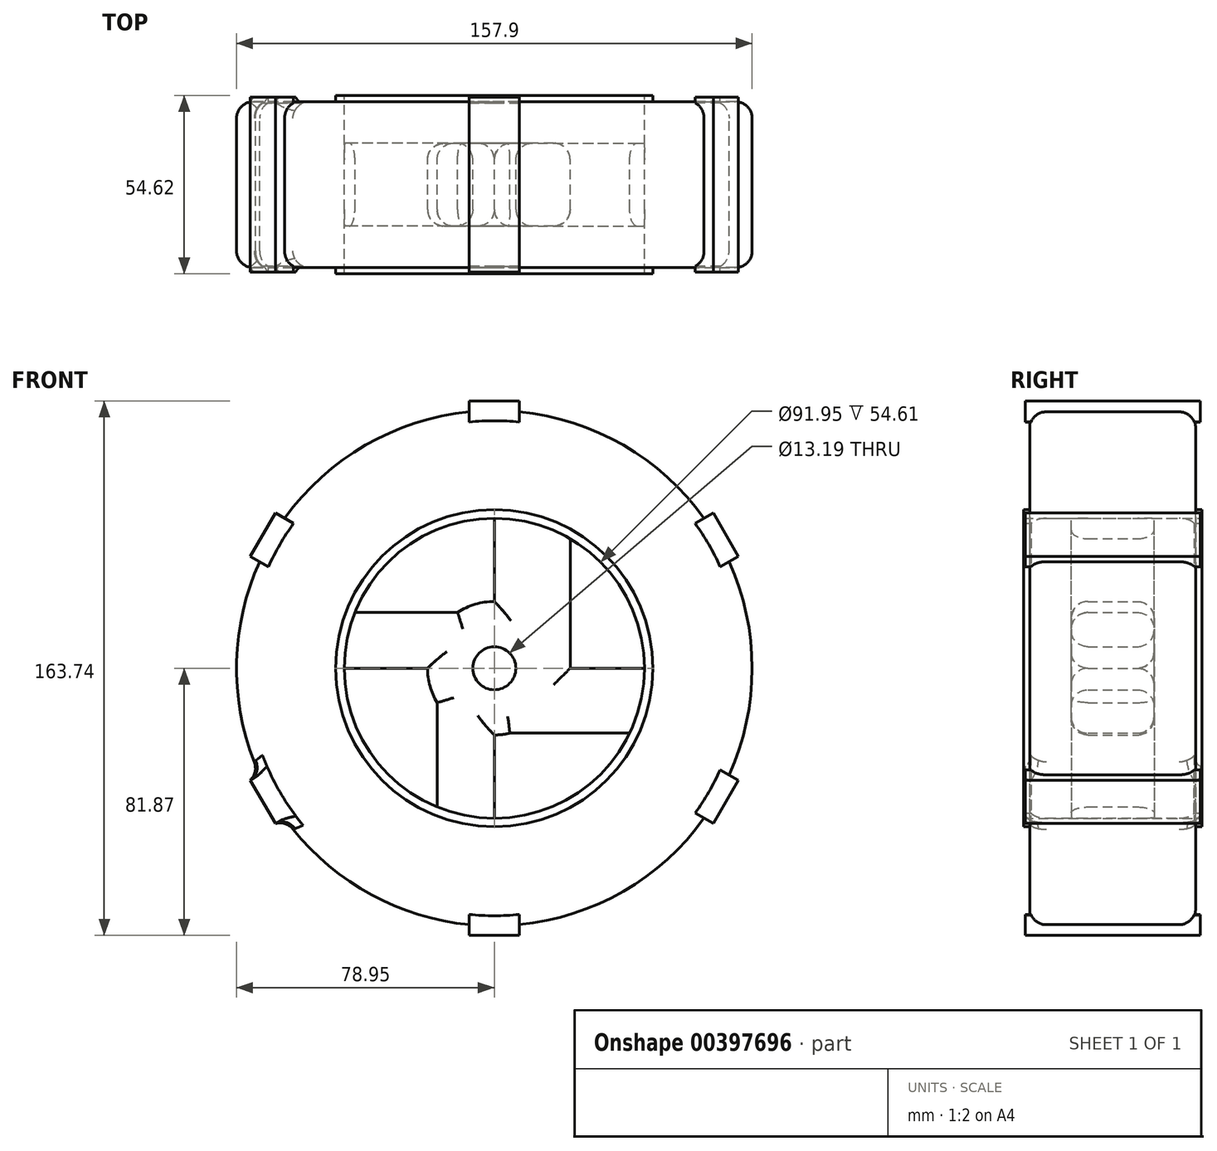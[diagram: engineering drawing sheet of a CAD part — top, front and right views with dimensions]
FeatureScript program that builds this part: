
annotation { "Feature Type Name" : "Feature", "Feature Type Description" : "" }
export const myFeature = defineFeature(function(context is Context, id is Id, definition is map)
    precondition{}
    {
        {
            var Q0;
            Q0=qCreatedBy(makeId("Front.planeOp"),FACE);
            var sketch = newSketch(context, id + "F0", { "sketchPlane" : qUnion([Q0])});
            skCircle(sketch, "E0", {"center": v(0, 0) * mm, "radius": 46.7 * mm});
            skCircle(sketch, "E1", {"center": v(0, 0) * mm, "radius": 78.95 * mm});
            skSolve(sketch);
        }
        {
            var Q0;
            Q0=makeQuery(id+"F0.imprint","IMPRINT",FACE,{"disambiguationData":[TD([[makeQuery(id+"F0.imprint","IMPRINT",EDGE,{"derivedFrom":sQuery(id+"F0.wireOp",EDGE,"E0")}),-1.0]])]});
            extrude(context, id + "F1", {"entities" : qUnion([Q0]), "endBound" : BoundingType.SYMMETRIC, "depth" : 50.8 * mm, "offsetDistance" : 25.4 * mm});
        }
        {
            var Q0;
            Q0=makeQuery(id+"F1.opExtrude","CAP_EDGE",EDGE,{"disambiguationData":[OSD([sQuery(id+"F0.wireOp",EDGE,"E1")])],"isStart":false});
            var Q1;
            Q1=makeQuery(id+"F1.opExtrude","SWEPT_FACE",FACE,{"disambiguationData":[OSD([sQuery(id+"F0.wireOp",EDGE,"E1")])]});
            fillet(context, id + "F2", {"entities" : qUnion([Q0, Q1]), "radius" : 5.08 * mm, "tangentPropagation" : true, "allowEdgeOverflow" : false});
        }
        {
            var Q0;
            Q0=qCreatedBy(makeId("Front.planeOp"),FACE);
            var sketch = newSketch(context, id + "F3", { "sketchPlane" : qUnion([Q0])});
            skCircle(sketch, "E2", {"center": v(0, 0) * mm, "radius": 48.57 * mm});
            skCircle(sketch, "E3", {"center": v(0, 0) * mm, "radius": 45.98 * mm});
            skSolve(sketch);
        }
        {
            var Q0;
            Q0 = qSketchRegion(id + "F3", true);
            extrude(context, id + "F4", {"entities" : qUnion([Q0]), "operationType" : NewBodyOperationType.ADD, "endBound" : BoundingType.SYMMETRIC, "depth" : 54.6 * mm, "offsetDistance" : 25.4 * mm});
        }
        {
            var Q0;
            Q0=qCreatedBy(makeId("Front.planeOp"),FACE);
            var sketch = newSketch(context, id + "F5", { "sketchPlane" : qUnion([Q0])});
            skCircle(sketch, "E4", {"center": v(0, 0) * mm, "radius": 20.45 * mm});
            skCircle(sketch, "E5", {"center": v(0, 0) * mm, "radius": 6.6 * mm});
            skLineSegment(sketch, "E6.bottom", {"start": v(0, 0) * mm, "end": v(53.17, 0) * mm});
            skLineSegment(sketch, "E6.top", {"start": v(0, -19.9) * mm, "end": v(53.17, -19.9) * mm});
            skLineSegment(sketch, "E6.left", {"start": v(0, 0) * mm, "end": v(0, -19.9) * mm});
            skLineSegment(sketch, "E6.right", {"start": v(53.17, 0) * mm, "end": v(53.17, -19.9) * mm});
            skLineSegment(sketch, "E7.bottom", {"start": v(0, 0) * mm, "end": v(-49.35, 0) * mm});
            skLineSegment(sketch, "E7.top", {"start": v(0, 17.09) * mm, "end": v(-49.35, 17.09) * mm});
            skLineSegment(sketch, "E7.left", {"start": v(0, 0) * mm, "end": v(0, 17.09) * mm});
            skLineSegment(sketch, "E7.right", {"start": v(-49.35, 0) * mm, "end": v(-49.35, 17.09) * mm});
            skLineSegment(sketch, "E8.bottom", {"start": v(0, 0) * mm, "end": v(-17.53, 0) * mm});
            skLineSegment(sketch, "E8.top", {"start": v(0, -48.72) * mm, "end": v(-17.53, -48.72) * mm});
            skLineSegment(sketch, "E8.left", {"start": v(0, 0) * mm, "end": v(0, -48.72) * mm});
            skLineSegment(sketch, "E8.right", {"start": v(-17.53, 0) * mm, "end": v(-17.53, -48.72) * mm});
            skLineSegment(sketch, "E9.bottom", {"start": v(0, 0) * mm, "end": v(23.22, 0) * mm});
            skLineSegment(sketch, "E9.top", {"start": v(0, 56.09) * mm, "end": v(23.22, 56.09) * mm});
            skLineSegment(sketch, "E9.left", {"start": v(0, 0) * mm, "end": v(0, 56.09) * mm});
            skLineSegment(sketch, "E9.right", {"start": v(23.22, 0) * mm, "end": v(23.22, 56.09) * mm});
            skSolve(sketch);
        }
        {
            var Q0;
            Q0 = qSketchRegion(id + "F5", true);
            extrude(context, id + "F6", {"entities" : qUnion([Q0]), "operationType" : NewBodyOperationType.ADD, "endBound" : BoundingType.SYMMETRIC, "depth" : 25.4 * mm, "offsetDistance" : 25.4 * mm});
        }
        {
            var Q0;
            Q0=makeQuery(id+"F6.opExtrude","CAP_EDGE",EDGE,{"disambiguationData":[OSD([sQuery(id+"F5.wireOp",EDGE,"E7.top")])],"isStart":false});
            var Q1;
            {var subQ0=sQuery(id+"F5.wireOp",EDGE,"E4");Q1=makeQuery(id+"F6.opExtrude","CAP_EDGE",EDGE,{"disambiguationData":[OSD([subQ0]),TDD([makeQuery(id+"F5.imprint","IMPRINT",EDGE,{"disambiguationData":[TD([[makeQuery(id+"F5.imprint","INTERSECT",VERTEX,{"derivedFrom":[subQ0,sQuery(id+"F5.wireOp",EDGE,"E9.left")]}),-1.0]])],"derivedFrom":subQ0})])],"isStart":false});}
            var Q2;
            Q2=makeQuery(id+"F6.opExtrude","CAP_EDGE",EDGE,{"disambiguationData":[OSD([sQuery(id+"F5.wireOp",EDGE,"E9.left")])],"isStart":false});
            var Q3;
            Q3=makeQuery(id+"F6.opExtrude","CAP_EDGE",EDGE,{"disambiguationData":[OSD([sQuery(id+"F5.wireOp",EDGE,"E9.right")])],"isStart":false});
            var Q4;
            Q4=makeQuery(id+"F6.opExtrude","CAP_EDGE",EDGE,{"disambiguationData":[OSD([sQuery(id+"F5.wireOp",EDGE,"E6.bottom")])],"isStart":false});
            var Q5;
            Q5=makeQuery(id+"F6.opExtrude","CAP_EDGE",EDGE,{"disambiguationData":[OSD([sQuery(id+"F5.wireOp",EDGE,"E6.top")])],"isStart":false});
            var Q6;
            Q6=makeQuery(id+"F6.opExtrude","CAP_EDGE",EDGE,{"disambiguationData":[OSD([sQuery(id+"F5.wireOp",EDGE,"E8.left")])],"isStart":false});
            var Q7;
            {var subQ0=sQuery(id+"F5.wireOp",EDGE,"E4");Q7=makeQuery(id+"F6.opExtrude","CAP_EDGE",EDGE,{"disambiguationData":[OSD([subQ0]),TDD([makeQuery(id+"F5.imprint","IMPRINT",EDGE,{"disambiguationData":[TD([[makeQuery(id+"F5.imprint","INTERSECT",VERTEX,{"derivedFrom":[subQ0,sQuery(id+"F5.wireOp",EDGE,"E8.left")]}),-1.0]])],"derivedFrom":subQ0})])],"isStart":false});}
            var Q8;
            Q8=makeQuery(id+"F6.opExtrude","CAP_EDGE",EDGE,{"disambiguationData":[OSD([sQuery(id+"F5.wireOp",EDGE,"E8.right")])],"isStart":false});
            var Q9;
            {var subQ0=sQuery(id+"F5.wireOp",EDGE,"E4");Q9=makeQuery(id+"F6.opExtrude","CAP_EDGE",EDGE,{"disambiguationData":[OSD([subQ0]),TDD([makeQuery(id+"F5.imprint","IMPRINT",EDGE,{"disambiguationData":[TD([[makeQuery(id+"F5.imprint","INTERSECT",VERTEX,{"derivedFrom":[subQ0,sQuery(id+"F5.wireOp",EDGE,"E7.bottom")]}),-1.0]])],"derivedFrom":subQ0})])],"isStart":false});}
            var Q10;
            Q10=makeQuery(id+"F6.opExtrude","CAP_EDGE",EDGE,{"disambiguationData":[OSD([sQuery(id+"F5.wireOp",EDGE,"E7.bottom")])],"isStart":false});
            var Q11;
            Q11=makeQuery(id+"F6.opExtrude","CAP_EDGE",EDGE,{"disambiguationData":[OSD([sQuery(id+"F5.wireOp",EDGE,"E9.left")])],"isStart":true});
            var Q12;
            {var subQ0=sQuery(id+"F5.wireOp",EDGE,"E4");Q12=makeQuery(id+"F6.opExtrude","CAP_EDGE",EDGE,{"disambiguationData":[OSD([subQ0]),TDD([makeQuery(id+"F5.imprint","IMPRINT",EDGE,{"disambiguationData":[TD([[makeQuery(id+"F5.imprint","INTERSECT",VERTEX,{"derivedFrom":[subQ0,sQuery(id+"F5.wireOp",EDGE,"E9.left")]}),-1.0]])],"derivedFrom":subQ0})])],"isStart":true});}
            var Q13;
            Q13=makeQuery(id+"F6.opExtrude","CAP_EDGE",EDGE,{"disambiguationData":[OSD([sQuery(id+"F5.wireOp",EDGE,"E7.top")])],"isStart":true});
            var Q14;
            Q14=makeQuery(id+"F6.opExtrude","CAP_EDGE",EDGE,{"disambiguationData":[OSD([sQuery(id+"F5.wireOp",EDGE,"E7.bottom")])],"isStart":true});
            var Q15;
            {var subQ0=sQuery(id+"F5.wireOp",EDGE,"E4");Q15=makeQuery(id+"F6.opExtrude","CAP_EDGE",EDGE,{"disambiguationData":[OSD([subQ0]),TDD([makeQuery(id+"F5.imprint","IMPRINT",EDGE,{"disambiguationData":[TD([[makeQuery(id+"F5.imprint","INTERSECT",VERTEX,{"derivedFrom":[subQ0,sQuery(id+"F5.wireOp",EDGE,"E7.bottom")]}),-1.0]])],"derivedFrom":subQ0})])],"isStart":true});}
            var Q16;
            Q16=makeQuery(id+"F6.opExtrude","CAP_EDGE",EDGE,{"disambiguationData":[OSD([sQuery(id+"F5.wireOp",EDGE,"E8.right")])],"isStart":true});
            var Q17;
            Q17=makeQuery(id+"F6.opExtrude","CAP_EDGE",EDGE,{"disambiguationData":[OSD([sQuery(id+"F5.wireOp",EDGE,"E8.left")])],"isStart":true});
            var Q18;
            {var subQ0=sQuery(id+"F5.wireOp",EDGE,"E4");Q18=makeQuery(id+"F6.opExtrude","CAP_EDGE",EDGE,{"disambiguationData":[OSD([subQ0]),TDD([makeQuery(id+"F5.imprint","IMPRINT",EDGE,{"disambiguationData":[TD([[makeQuery(id+"F5.imprint","INTERSECT",VERTEX,{"derivedFrom":[subQ0,sQuery(id+"F5.wireOp",EDGE,"E8.left")]}),-1.0]])],"derivedFrom":subQ0})])],"isStart":true});}
            var Q19;
            Q19=makeQuery(id+"F6.opExtrude","CAP_EDGE",EDGE,{"disambiguationData":[OSD([sQuery(id+"F5.wireOp",EDGE,"E6.top")])],"isStart":true});
            var Q20;
            Q20=makeQuery(id+"F6.opExtrude","CAP_EDGE",EDGE,{"disambiguationData":[OSD([sQuery(id+"F5.wireOp",EDGE,"E6.bottom")])],"isStart":true});
            var Q21;
            Q21=makeQuery(id+"F6.opExtrude","CAP_EDGE",EDGE,{"disambiguationData":[OSD([sQuery(id+"F5.wireOp",EDGE,"E9.right")])],"isStart":true});
            var Q22;
            Q22=makeQuery(id+"F6.opExtrude","CAP_EDGE",EDGE,{"disambiguationData":[OSD([sQuery(id+"F5.wireOp",EDGE,"E5")])],"isStart":true});
            var Q23;
            Q23=makeQuery(id+"F6.opExtrude","CAP_EDGE",EDGE,{"disambiguationData":[OSD([sQuery(id+"F5.wireOp",EDGE,"E5")])],"isStart":false});
            fillet(context, id + "F7", {"entities" : qUnion([Q0, Q1, Q2, Q3, Q4, Q5, Q6, Q7, Q8, Q9, Q10, Q11, Q12, Q13, Q14, Q15, Q16, Q17, Q18, Q19, Q20, Q21, Q22, Q23]), "radius" : 5.08 * mm, "tangentPropagation" : true, "allowEdgeOverflow" : false});
        }
        {
            var Q0;
            Q0=qCreatedBy(makeId("Front.planeOp"),FACE);
            var sketch = newSketch(context, id + "F8", { "sketchPlane" : qUnion([Q0])});
            skLineSegment(sketch, "E10.bottom", {"start": v(-7.66, 81.87) * mm, "end": v(7.66, 81.87) * mm});
            skLineSegment(sketch, "E10.top", {"start": v(-7.66, -81.87) * mm, "end": v(7.66, -81.87) * mm});
            skLineSegment(sketch, "E10.left", {"start": v(-7.66, 81.87) * mm, "end": v(-7.66, -81.87) * mm});
            skLineSegment(sketch, "E10.right", {"start": v(7.66, 81.87) * mm, "end": v(7.66, -81.87) * mm});
            skPoint(sketch, "E10.middle", {"position": v(0, 0) * mm});
            skCircle(sketch, "E11", {"center": v(0, 0) * mm, "radius": 75.83 * mm});
            skLineSegment(sketch, "E12.1.0", {"start": v(-67.07, -47.57) * mm, "end": v(-74.73, -34.3) * mm});
            skLineSegment(sketch, "E12.1.1", {"start": v(-74.73, -34.3) * mm, "end": v(67.07, 47.57) * mm});
            skLineSegment(sketch, "E12.1.2", {"start": v(-67.07, -47.57) * mm, "end": v(74.73, 34.3) * mm});
            skLineSegment(sketch, "E12.1.3", {"start": v(74.73, 34.3) * mm, "end": v(67.07, 47.57) * mm});
            skLineSegment(sketch, "E12.2.0", {"start": v(74.73, -34.3) * mm, "end": v(67.07, -47.57) * mm});
            skLineSegment(sketch, "E12.2.1", {"start": v(67.07, -47.57) * mm, "end": v(-74.73, 34.3) * mm});
            skLineSegment(sketch, "E12.2.2", {"start": v(74.73, -34.3) * mm, "end": v(-67.07, 47.57) * mm});
            skLineSegment(sketch, "E12.2.3", {"start": v(-67.07, 47.57) * mm, "end": v(-74.73, 34.3) * mm});
            skSolve(sketch);
        }
        {
            var Q0;
            {var subQ0=sQuery(id+"F8.wireOp",EDGE,"E10.bottom");Q0=makeQuery(id+"F8.imprint","IMPRINT",FACE,{"disambiguationData":[TD([[makeQuery(id+"F8.imprint","IMPRINT",EDGE,{"derivedFrom":subQ0}),-1.0]])]});}
            var Q1;
            {var subQ5=sQuery(id+"F8.wireOp",EDGE,"E12.2.3");Q1=makeQuery(id+"F8.imprint","IMPRINT",FACE,{"disambiguationData":[TD([[makeQuery(id+"F8.imprint","IMPRINT",EDGE,{"derivedFrom":subQ5}),1.0]])]});}
            var Q2;
            {var subQ5=sQuery(id+"F8.wireOp",EDGE,"E12.1.0");Q2=makeQuery(id+"F8.imprint","IMPRINT",FACE,{"disambiguationData":[TD([[makeQuery(id+"F8.imprint","IMPRINT",EDGE,{"derivedFrom":subQ5}),-1.0]])]});}
            var Q3;
            {var subQ0=sQuery(id+"F8.wireOp",EDGE,"E10.top");Q3=makeQuery(id+"F8.imprint","IMPRINT",FACE,{"disambiguationData":[TD([[makeQuery(id+"F8.imprint","IMPRINT",EDGE,{"derivedFrom":subQ0}),1.0]])]});}
            var Q4;
            {var subQ5=sQuery(id+"F8.wireOp",EDGE,"E12.2.0");Q4=makeQuery(id+"F8.imprint","IMPRINT",FACE,{"disambiguationData":[TD([[makeQuery(id+"F8.imprint","IMPRINT",EDGE,{"derivedFrom":subQ5}),-1.0]])]});}
            var Q5;
            {var subQ5=sQuery(id+"F8.wireOp",EDGE,"E12.1.3");Q5=makeQuery(id+"F8.imprint","IMPRINT",FACE,{"disambiguationData":[TD([[makeQuery(id+"F8.imprint","IMPRINT",EDGE,{"derivedFrom":subQ5}),1.0]])]});}
            extrude(context, id + "F9", {"entities" : qUnion([Q0, Q1, Q2, Q3, Q4, Q5]), "operationType" : NewBodyOperationType.ADD, "endBound" : BoundingType.SYMMETRIC, "depth" : 53.6 * mm, "offsetDistance" : 25.4 * mm});
        }
        {
            var Q0;
            {var subQ0=sQuery(id+"F8.wireOp",EDGE,"E12.1.2");Q0=makeQuery(id+"F9.boolean.opBoolean","INTERSECT",EDGE,{"derivedFrom":[makeQuery(id+"F1.opExtrude","SWEPT_FACE",FACE,{"disambiguationData":[OSD([sQuery(id+"F0.wireOp",EDGE,"E1")])]}),makeQuery(id+"F9.opExtrude","SWEPT_FACE",FACE,{"disambiguationData":[OSD([subQ0]),TDD([makeQuery(id+"F8.imprint","IMPRINT",EDGE,{"disambiguationData":[TD([[makeQuery(id+"F8.imprint","INTERSECT",VERTEX,{"derivedFrom":[sQuery(id+"F8.wireOp",EDGE,"E12.1.0"),subQ0]}),-1.0]])],"derivedFrom":subQ0})])]})]});}
            var Q1;
            {var subQ0=sQuery(id+"F8.wireOp",EDGE,"E11");var subQ1=sQuery(id+"F0.wireOp",EDGE,"E1");Q1=makeQuery(id+"F9.boolean.opBoolean","INTERSECT",EDGE,{"derivedFrom":[makeQuery(id+"F2.opFillet","BLEND_FACE",FACE,{"disambiguationData":[OSD([subQ1]),TDD([makeQuery(id+"F1.opExtrude","CAP_EDGE",EDGE,{"disambiguationData":[OSD([subQ1])],"isStart":false})])]}),makeQuery(id+"F9.opExtrude","SWEPT_FACE",FACE,{"disambiguationData":[OSD([subQ0]),TDD([makeQuery(id+"F8.imprint","IMPRINT",EDGE,{"disambiguationData":[TD([[makeQuery(id+"F8.imprint","INTERSECT",VERTEX,{"disambiguationData":[OD(1.0)],"derivedFrom":[subQ0,sQuery(id+"F8.wireOp",EDGE,"E12.1.1")]}),-1.0]])],"derivedFrom":subQ0})])]})]});}
            var Q2;
            {var subQ0=sQuery(id+"F8.wireOp",EDGE,"E12.1.1");var subQ1=sQuery(id+"F0.wireOp",EDGE,"E1");Q2=makeQuery(id+"F9.boolean.opBoolean","INTERSECT",EDGE,{"derivedFrom":[makeQuery(id+"F2.opFillet","BLEND_FACE",FACE,{"disambiguationData":[OSD([subQ1]),TDD([makeQuery(id+"F1.opExtrude","CAP_EDGE",EDGE,{"disambiguationData":[OSD([subQ1])],"isStart":false})])]}),makeQuery(id+"F9.opExtrude","SWEPT_FACE",FACE,{"disambiguationData":[OSD([subQ0]),TDD([makeQuery(id+"F8.imprint","IMPRINT",EDGE,{"disambiguationData":[TD([[makeQuery(id+"F8.imprint","INTERSECT",VERTEX,{"derivedFrom":[sQuery(id+"F8.wireOp",EDGE,"E12.1.0"),subQ0]}),-1.0]])],"derivedFrom":subQ0})])]})]});}
            var Q3;
            {var subQ0=sQuery(id+"F8.wireOp",EDGE,"E12.1.1");Q3=makeQuery(id+"F9.boolean.opBoolean","INTERSECT",EDGE,{"derivedFrom":[makeQuery(id+"F1.opExtrude","SWEPT_FACE",FACE,{"disambiguationData":[OSD([sQuery(id+"F0.wireOp",EDGE,"E1")])]}),makeQuery(id+"F9.opExtrude","SWEPT_FACE",FACE,{"disambiguationData":[OSD([subQ0]),TDD([makeQuery(id+"F8.imprint","IMPRINT",EDGE,{"disambiguationData":[TD([[makeQuery(id+"F8.imprint","INTERSECT",VERTEX,{"derivedFrom":[sQuery(id+"F8.wireOp",EDGE,"E12.1.0"),subQ0]}),-1.0]])],"derivedFrom":subQ0})])]})]});}
            var Q4;
            {var subQ0=sQuery(id+"F8.wireOp",EDGE,"E11");var subQ1=sQuery(id+"F0.wireOp",EDGE,"E1");Q4=makeQuery(id+"F9.boolean.opBoolean","INTERSECT",EDGE,{"derivedFrom":[makeQuery(id+"F2.opFillet","BLEND_FACE",FACE,{"disambiguationData":[OSD([subQ1]),TDD([makeQuery(id+"F1.opExtrude","CAP_EDGE",EDGE,{"disambiguationData":[OSD([subQ1])],"isStart":true})])]}),makeQuery(id+"F9.opExtrude","SWEPT_FACE",FACE,{"disambiguationData":[OSD([subQ0]),TDD([makeQuery(id+"F8.imprint","IMPRINT",EDGE,{"disambiguationData":[TD([[makeQuery(id+"F8.imprint","INTERSECT",VERTEX,{"disambiguationData":[OD(1.0)],"derivedFrom":[subQ0,sQuery(id+"F8.wireOp",EDGE,"E12.1.1")]}),-1.0]])],"derivedFrom":subQ0})])]})]});}
            var Q5;
            {var subQ0=sQuery(id+"F8.wireOp",EDGE,"E12.1.2");var subQ1=sQuery(id+"F0.wireOp",EDGE,"E1");Q5=makeQuery(id+"F9.boolean.opBoolean","INTERSECT",EDGE,{"derivedFrom":[makeQuery(id+"F2.opFillet","BLEND_FACE",FACE,{"disambiguationData":[OSD([subQ1]),TDD([makeQuery(id+"F1.opExtrude","CAP_EDGE",EDGE,{"disambiguationData":[OSD([subQ1])],"isStart":true})])]}),makeQuery(id+"F9.opExtrude","SWEPT_FACE",FACE,{"disambiguationData":[OSD([subQ0]),TDD([makeQuery(id+"F8.imprint","IMPRINT",EDGE,{"disambiguationData":[TD([[makeQuery(id+"F8.imprint","INTERSECT",VERTEX,{"derivedFrom":[sQuery(id+"F8.wireOp",EDGE,"E12.1.0"),subQ0]}),-1.0]])],"derivedFrom":subQ0})])]})]});}
            var Q6;
            {var subQ0=sQuery(id+"F8.wireOp",EDGE,"E12.1.1");var subQ1=sQuery(id+"F0.wireOp",EDGE,"E1");Q6=makeQuery(id+"F9.boolean.opBoolean","INTERSECT",EDGE,{"derivedFrom":[makeQuery(id+"F2.opFillet","BLEND_FACE",FACE,{"disambiguationData":[OSD([subQ1]),TDD([makeQuery(id+"F1.opExtrude","CAP_EDGE",EDGE,{"disambiguationData":[OSD([subQ1])],"isStart":true})])]}),makeQuery(id+"F9.opExtrude","SWEPT_FACE",FACE,{"disambiguationData":[OSD([subQ0]),TDD([makeQuery(id+"F8.imprint","IMPRINT",EDGE,{"disambiguationData":[TD([[makeQuery(id+"F8.imprint","INTERSECT",VERTEX,{"derivedFrom":[sQuery(id+"F8.wireOp",EDGE,"E12.1.0"),subQ0]}),-1.0]])],"derivedFrom":subQ0})])]})]});}
            var Q7;
            {var subQ0=sQuery(id+"F8.wireOp",EDGE,"E11");Q7=makeQuery(id+"F9.opExtrude","CAP_EDGE",EDGE,{"disambiguationData":[OSD([subQ0]),TDD([makeQuery(id+"F8.imprint","IMPRINT",EDGE,{"disambiguationData":[TD([[makeQuery(id+"F8.imprint","INTERSECT",VERTEX,{"disambiguationData":[OD(1.0)],"derivedFrom":[subQ0,sQuery(id+"F8.wireOp",EDGE,"E12.1.1")]}),-1.0]])],"derivedFrom":subQ0})])],"isStart":false});}
            var Q8;
            {var subQ0=sQuery(id+"F8.wireOp",EDGE,"E12.1.2");var subQ1=sQuery(id+"F0.wireOp",EDGE,"E1");Q8=makeQuery(id+"F9.boolean.opBoolean","INTERSECT",EDGE,{"derivedFrom":[makeQuery(id+"F2.opFillet","BLEND_FACE",FACE,{"disambiguationData":[OSD([subQ1]),TDD([makeQuery(id+"F1.opExtrude","CAP_EDGE",EDGE,{"disambiguationData":[OSD([subQ1])],"isStart":false})])]}),makeQuery(id+"F9.opExtrude","SWEPT_FACE",FACE,{"disambiguationData":[OSD([subQ0]),TDD([makeQuery(id+"F8.imprint","IMPRINT",EDGE,{"disambiguationData":[TD([[makeQuery(id+"F8.imprint","INTERSECT",VERTEX,{"derivedFrom":[sQuery(id+"F8.wireOp",EDGE,"E12.1.0"),subQ0]}),-1.0]])],"derivedFrom":subQ0})])]})]});}
            fillet(context, id + "F10", {"entities" : qUnion([Q0, Q1, Q2, Q3, Q4, Q5, Q6, Q7, Q8]), "radius" : 5.08 * mm, "tangentPropagation" : true, "allowEdgeOverflow" : false});
        }
    });
